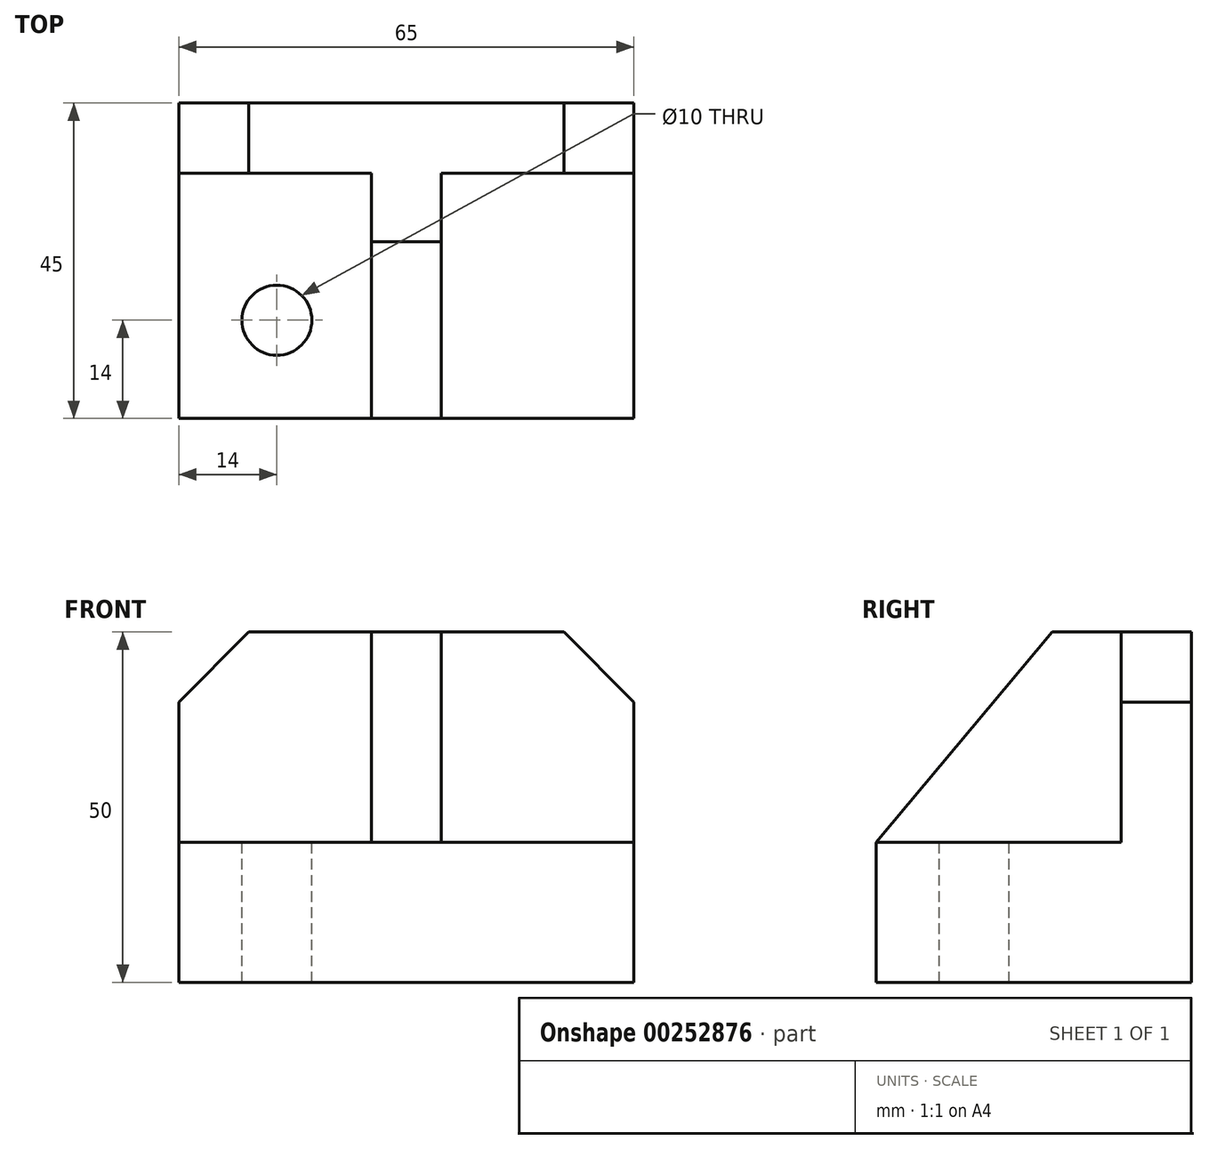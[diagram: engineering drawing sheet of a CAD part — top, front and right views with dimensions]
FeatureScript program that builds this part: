
annotation { "Feature Type Name" : "Feature", "Feature Type Description" : "" }
export const myFeature = defineFeature(function(context is Context, id is Id, definition is map)
    precondition{}
    {
        {
            var Q0;
            Q0=qCreatedBy(makeId("Front.planeOp"),FACE);
            var sketch = newSketch(context, id + "F0", { "sketchPlane" : qUnion([Q0])});
            skLineSegment(sketch, "E0.bottom", {"start": v(32.5, -25) * mm, "end": v(-32.5, -25) * mm});
            skLineSegment(sketch, "E0.top", {"start": v(32.5, 25) * mm, "end": v(-32.5, 25) * mm});
            skLineSegment(sketch, "E0.left", {"start": v(32.5, -25) * mm, "end": v(32.5, 25) * mm});
            skLineSegment(sketch, "E0.right", {"start": v(-32.5, -25) * mm, "end": v(-32.5, 25) * mm});
            skPoint(sketch, "E0.middle", {"position": v(0, 0) * mm});
            skSolve(sketch);
        }
        {
            var Q0;
            Q0=makeQuery(id+"F0.imprint","IMPRINT",FACE,{"disambiguationData":[TD([[makeQuery(id+"F0.imprint","IMPRINT",EDGE,{"derivedFrom":sQuery(id+"F0.wireOp",EDGE,"E0.bottom")}),-1.0]])]});
            extrude(context, id + "F1", {"entities" : qUnion([Q0]), "depth" : 10 * mm});
        }
        {
            var Q0;
            Q0=makeQuery(id+"F1.opExtrude","CAP_FACE",FACE,{"disambiguationData":[OSD([sQuery(id+"F0.wireOp",EDGE,"E0.bottom"),sQuery(id+"F0.wireOp",EDGE,"E0.top"),sQuery(id+"F0.wireOp",EDGE,"E0.left"),sQuery(id+"F0.wireOp",EDGE,"E0.right")])],"isStart":false});
            var sketch = newSketch(context, id + "F2", { "sketchPlane" : qUnion([Q0])});
            skLineSegment(sketch, "E1.bottom", {"start": v(-32.5, -25) * mm, "end": v(32.5, -25) * mm});
            skLineSegment(sketch, "E1.top", {"start": v(-32.5, -5) * mm, "end": v(32.5, -5) * mm});
            skLineSegment(sketch, "E1.left", {"start": v(-32.5, -25) * mm, "end": v(-32.5, -5) * mm});
            skLineSegment(sketch, "E1.right", {"start": v(32.5, -25) * mm, "end": v(32.5, -5) * mm});
            skSolve(sketch);
        }
        {
            var Q0;
            Q0=makeQuery(id+"F2.imprint","IMPRINT",FACE,{"disambiguationData":[TD([[makeQuery(id+"F2.imprint","IMPRINT",EDGE,{"derivedFrom":sQuery(id+"F2.wireOp",EDGE,"E1.bottom")}),-1.0]])]});
            extrude(context, id + "F3", {"entities" : qUnion([Q0]), "operationType" : NewBodyOperationType.ADD, "depth" : 35 * mm});
        }
        {
            var Q0;
            Q0=qCreatedBy(makeId("Right.planeOp"),FACE);
            var sketch = newSketch(context, id + "F4", { "sketchPlane" : qUnion([Q0])});
            skLineSegment(sketch, "E2.0", {"start": v(-10, -5) * mm, "end": v(-10, 25) * mm});
            skLineSegment(sketch, "E3.0", {"start": v(-45, -5) * mm, "end": v(-10, -5) * mm});
            skLineSegment(sketch, "E4", {"start": v(-10, 25) * mm, "end": v(-19.83, 25) * mm});
            skLineSegment(sketch, "E5", {"start": v(-19.83, 25) * mm, "end": v(-45, -5) * mm});
            skSolve(sketch);
        }
        {
            var Q0;
            Q0=makeQuery(id+"F4.imprint","IMPRINT",FACE,{"disambiguationData":[TD([[makeQuery(id+"F4.imprint","IMPRINT",EDGE,{"derivedFrom":sQuery(id+"F4.wireOp",EDGE,"E2.0")}),1.0]])]});
            extrude(context, id + "F5", {"entities" : qUnion([Q0]), "operationType" : NewBodyOperationType.ADD, "depth" : 10 * mm, "symmetric" : true});
        }
        {
            var Q0;
            Q0=makeQuery(id+"F1.opExtrude","SWEPT_EDGE",EDGE,{"disambiguationData":[OSD([sQuery(id+"F0.wireOp",EDGE,"E0.top"),sQuery(id+"F0.wireOp",EDGE,"E0.right")])]});
            var Q1;
            Q1=makeQuery(id+"F1.opExtrude","SWEPT_EDGE",EDGE,{"disambiguationData":[OSD([sQuery(id+"F0.wireOp",EDGE,"E0.top"),sQuery(id+"F0.wireOp",EDGE,"E0.left")])]});
            chamfer(context, id + "F6", {"entities" : qUnion([Q0, Q1]), "width" : 10 * mm, "tangentPropagation" : true});
        }
        {
            var Q0;
            {var subQ1=sQuery(id+"F2.wireOp",EDGE,"E1.top");var subQ3=sQuery(id+"F0.wireOp",EDGE,"E0.right");Q0=makeQuery(id+"F5.boolean.opBoolean","SPLIT",FACE,{"disambiguationData":[TD([makeQuery(id+"F1.opExtrude","SWEPT_FACE",FACE,{"disambiguationData":[OSD([subQ3])]})])],"derivedFrom":makeQuery(id+"F3.opExtrude","SWEPT_FACE",FACE,{"disambiguationData":[OSD([subQ1])]})});}
            var sketch = newSketch(context, id + "F7", { "sketchPlane" : qUnion([Q0])});
            skCircle(sketch, "E6", {"center": v(-18.5, -31) * mm, "radius": 5 * mm});
            skCircle(sketch, "E7.MirrorC", {"center": v(18.5, -31) * mm, "radius": 5 * mm});
            skSolve(sketch);
        }
        {
            var Q0;
            Q0=makeQuery(id+"F7.imprint","IMPRINT",FACE,{"disambiguationData":[TD([[makeQuery(id+"F7.imprint","IMPRINT",EDGE,{"derivedFrom":sQuery(id+"F7.wireOp",EDGE,"E6")}),1.0]])]});
            var Q1;
            Q1=makeQuery(id+"F7.imprint","IMPRINT",FACE,{"disambiguationData":[TD([[makeQuery(id+"F7.imprint","IMPRINT",EDGE,{"derivedFrom":sQuery(id+"F7.wireOp",EDGE,"E7.MirrorC")}),-1.0]])]});
            extrude(context, id + "F8", {"entities" : qUnion([Q0, Q1]), "operationType" : NewBodyOperationType.REMOVE, "endBound" : BoundingType.THROUGH_ALL, "oppositeDirection" : true, "depth" : 25 * mm});
        }
    });
